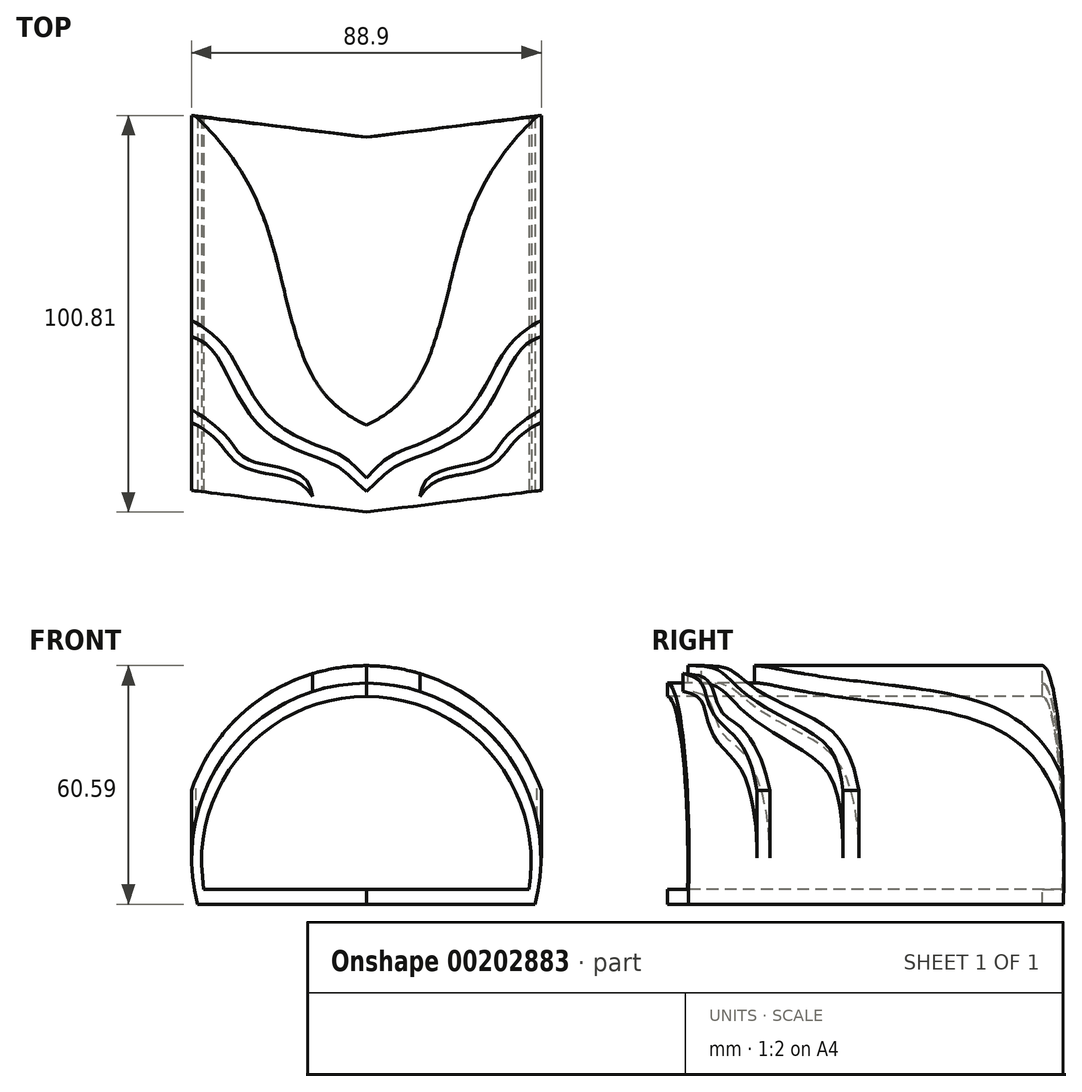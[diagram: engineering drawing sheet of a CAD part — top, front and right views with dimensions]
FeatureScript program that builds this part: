
annotation { "Feature Type Name" : "Feature", "Feature Type Description" : "" }
export const myFeature = defineFeature(function(context is Context, id is Id, definition is map)
    precondition{}
    {
        {
            var Q0;
            Q0=qCreatedBy(makeId("Front.planeOp"),FACE);
            var sketch = newSketch(context, id + "F0", { "sketchPlane" : qUnion([Q0])});
            skLineSegment(sketch, "E0", {"start": v(-42.86, 0) * mm, "end": v(42.86, 0) * mm});
            skArc(sketch, "E1", {"start": v(42.86, 0) * mm, "mid": v(0, 56.22) * mm, "end": v(-42.86, 0) * mm});
            skSolve(sketch);
        }
        {
            var Q0;
            Q0=makeQuery(id+"F0.imprint","IMPRINT",FACE,{"disambiguationData":[TD([[makeQuery(id+"F0.imprint","IMPRINT",EDGE,{"derivedFrom":sQuery(id+"F0.wireOp",EDGE,"E0")}),1.0]])]});
            extrude(context, id + "F1", {"entities" : qUnion([Q0]), "endBound" : BoundingType.SYMMETRIC, "oppositeDirection" : true, "depth" : 101.6 * mm});
        }
        {
            var Q0;
            Q0=qCreatedBy(makeId("Top.planeOp"),FACE);
            cPlane(context, id + "F2", {"entities" : qUnion([Q0]), "cplaneType" : CPlaneType.OFFSET, "offset" : 76.2 * mm, "width" : 152.4 * mm, "height" : 152.4 * mm});
        }
        {
            var Q0;
            Q0=qCreatedBy(id+"F2.planeOp",FACE);
            var sketch = newSketch(context, id + "F3", { "sketchPlane" : qUnion([Q0])});
            skLineSegment(sketch, "E2", {"start": v(-50.8, -44.45) * mm, "end": v(50.8, -44.45) * mm});
            skLineSegment(sketch, "E3", {"start": v(-50.8, -44.45) * mm, "end": v(0, -50.8) * mm});
            skLineSegment(sketch, "E4", {"start": v(0, -50.8) * mm, "end": v(50.8, -44.45) * mm});
            skLineSegment(sketch, "E5", {"start": v(-50.8, 50.8) * mm, "end": v(50.8, 50.8) * mm});
            skLineSegment(sketch, "E6", {"start": v(-50.8, 50.8) * mm, "end": v(0, 44.45) * mm});
            skLineSegment(sketch, "E7", {"start": v(0, 44.45) * mm, "end": v(50.8, 50.8) * mm});
            skLineSegment(sketch, "E8", {"start": v(-50.8, -44.45) * mm, "end": v(-50.8, -60.54) * mm});
            skLineSegment(sketch, "E9", {"start": v(0, -50.8) * mm, "end": v(-68, -50.8) * mm});
            skLineSegment(sketch, "E10", {"start": v(0, -50.8) * mm, "end": v(79.55, -50.8) * mm});
            skLineSegment(sketch, "E11", {"start": v(50.8, -44.45) * mm, "end": v(50.8, -63.1) * mm});
            skSolve(sketch);
        }
        {
            var Q0;
            {var subQ0=sQuery(id+"F3.wireOp",EDGE,"E4");Q0=makeQuery(id+"F3.imprint","IMPRINT",FACE,{"disambiguationData":[TD([[makeQuery(id+"F3.imprint","IMPRINT",EDGE,{"derivedFrom":subQ0}),-1.0]])]});}
            var Q1;
            {var subQ0=sQuery(id+"F3.wireOp",EDGE,"E3");Q1=makeQuery(id+"F3.imprint","IMPRINT",FACE,{"disambiguationData":[TD([[makeQuery(id+"F3.imprint","IMPRINT",EDGE,{"derivedFrom":subQ0}),-1.0]])]});}
            var Q2;
            Q2=makeQuery(id+"F3.imprint","IMPRINT",FACE,{"disambiguationData":[TD([[makeQuery(id+"F3.imprint","IMPRINT",EDGE,{"derivedFrom":sQuery(id+"F3.wireOp",EDGE,"E5")}),-1.0]])]});
            extrude(context, id + "F4", {"entities" : qUnion([Q0, Q1, Q2]), "operationType" : NewBodyOperationType.REMOVE, "endBound" : BoundingType.THROUGH_ALL, "oppositeDirection" : true, "depth" : 25.4 * mm});
        }
        {
            var Q0;
            Q0=qCreatedBy(makeId("Top.planeOp"),FACE);
            cPlane(context, id + "F5", {"entities" : qUnion([Q0]), "cplaneType" : CPlaneType.OFFSET, "offset" : 63.5 * mm, "width" : 152.4 * mm, "height" : 152.4 * mm});
        }
        {
            var Q0;
            Q0=qCreatedBy(makeId("Front.planeOp"),FACE);
            cPlane(context, id + "F6", {"entities" : qUnion([Q0]), "cplaneType" : CPlaneType.OFFSET, "offset" : 63.5 * mm, "width" : 152.4 * mm, "height" : 152.4 * mm});
        }
        {
            var Q0;
            Q0=qCreatedBy(id+"F5.planeOp",FACE);
            var sketch = newSketch(context, id + "F7", { "sketchPlane" : qUnion([Q0])});
            skLineSegment(sketch, "E12", {"start": v(0, 44.45) * mm, "end": v(0, -50.8) * mm, "construction": true});
            skLineSegment(sketch, "E13.bottom", {"start": v(0, -50.8) * mm, "end": v(44.45, -50.8) * mm, "construction": true});
            skLineSegment(sketch, "E13.top", {"start": v(0, 50.8) * mm, "end": v(44.45, 50.8) * mm, "construction": true});
            skLineSegment(sketch, "E13.left", {"start": v(0, -50.8) * mm, "end": v(0, 50.8) * mm, "construction": true});
            skLineSegment(sketch, "E13.right", {"start": v(44.45, -50.8) * mm, "end": v(44.45, 50.8) * mm, "construction": true});
            skFitSpline(sketch, "E14", {"points": [v(0, -28.69) * mm, v(17.05, -8.34) * mm, v(23.1, 14.39) * mm, v(44.45, 50.8) * mm], "startDerivative": vector(102.18, 47.54) * mm, "endDerivative": vector(107.88, 98.84) * mm});
            skLineSegment(sketch, "E15", {"start": v(0, 44.45) * mm, "end": v(43.3, 49.72) * mm, "construction": true});
            skFitSpline(sketch, "E16", {"points": [v(0, -45.55) * mm, v(3.85, -42.07) * mm, v(8.07, -38.77) * mm, v(26.4, -29.6) * mm, v(38.68, -10.17) * mm, v(44.45, -6.14) * mm], "startDerivative": vector(28.52, 26.1) * mm, "endDerivative": vector(36.73, 15.42) * mm});
            skFitSpline(sketch, "E17", {"points": [v(0, -42.07) * mm, v(3.3, -38.77) * mm, v(7.52, -35.83) * mm, v(23.65, -27.59) * mm, v(35.38, -9.62) * mm, v(44.45, -2.1) * mm], "startDerivative": vector(19.75, 23.3) * mm, "endDerivative": vector(48.33, 24.55) * mm});
            skFitSpline(sketch, "E18", {"points": [v(10.43, -20.94) * mm, v(21.08, -12.92) * mm, v(31.17, 3.57) * mm, v(44.45, 12.74) * mm], "startDerivative": vector(37.89, 20.7) * mm, "endDerivative": vector(43.58, 21.64) * mm});
            skFitSpline(sketch, "E19", {"points": [v(13.93, -15.76) * mm, v(19.8, -10.36) * mm, v(27.87, 4.5) * mm, v(44.45, 16.22) * mm], "startDerivative": vector(25.1, 17.01) * mm, "endDerivative": vector(47.74, 24.91) * mm});
            skFitSpline(sketch, "E20", {"points": [v(21.08, 6.33) * mm, v(26.22, 12) * mm, v(28.78, 20.07) * mm, v(36.66, 29.24) * mm, v(44.45, 33.64) * mm], "startDerivative": vector(27.07, 22.58) * mm, "endDerivative": vector(31.22, 14.61) * mm});
            skFitSpline(sketch, "E21", {"points": [v(22.43, 11.8) * mm, v(25.17, 16.63) * mm, v(27.6, 22.21) * mm, v(35.65, 31.39) * mm, v(44.45, 36.2) * mm], "startDerivative": vector(18.51, 3.78) * mm, "endDerivative": vector(31.7, 14.95) * mm});
            skFitSpline(sketch, "E22", {"points": [v(13.66, -46.82) * mm, v(16.5, -43.72) * mm, v(21.78, -41.65) * mm, v(32.07, -38.83) * mm, v(37.76, -32.72) * mm, v(44.45, -27.95) * mm], "startDerivative": vector(18.19, 23.47) * mm, "endDerivative": vector(36.32, 19.04) * mm});
            skFitSpline(sketch, "E23", {"points": [v(13.66, -46.82) * mm, v(14.9, -43) * mm, v(20.92, -39.76) * mm, v(30.81, -37.08) * mm, v(34.72, -32.57) * mm, v(44.45, -24.75) * mm], "startDerivative": vector(6.16, 28.42) * mm, "endDerivative": vector(47.3, 26.68) * mm});
            skLineSegment(sketch, "E24", {"start": v(0, -50.8) * mm, "end": v(0, 44.45) * mm});
            skLineSegment(sketch, "E25", {"start": v(0, 44.45) * mm, "end": v(43.3, 49.72) * mm});
            skLineSegment(sketch, "E26", {"start": v(0, -50.8) * mm, "end": v(44.45, -50.8) * mm});
            skLineSegment(sketch, "E27", {"start": v(44.45, -50.8) * mm, "end": v(44.45, 50.8) * mm});
            skLineSegment(sketch, "E28.MirrorCS", {"start": v(-44.45, -50.8) * mm, "end": v(-44.45, 50.8) * mm});
            skLineSegment(sketch, "E29.MirrorCS", {"start": v(0, -50.8) * mm, "end": v(-44.45, -50.8) * mm});
            skLineSegment(sketch, "E30.MirrorCS", {"start": v(0, 44.45) * mm, "end": v(-43.3, 49.72) * mm});
            skLineSegment(sketch, "E31.MirrorCS", {"start": v(0, 50.8) * mm, "end": v(-44.45, 50.8) * mm, "construction": true});
            skLineSegment(sketch, "E32.MirrorCS", {"start": v(-44.45, -50.8) * mm, "end": v(-44.45, 50.8) * mm, "construction": true});
            skFitSpline(sketch, "E33.MirrorCS", {"points": [v(0, -28.69) * mm, v(-17.05, -8.34) * mm, v(-23.1, 14.39) * mm, v(-44.45, 50.8) * mm], "startDerivative": vector(-102.18, 47.54) * mm, "endDerivative": vector(-107.88, 98.84) * mm});
            skLineSegment(sketch, "E34.MirrorCS", {"start": v(0, -50.8) * mm, "end": v(-44.45, -50.8) * mm, "construction": true});
            skLineSegment(sketch, "E35.MirrorCS", {"start": v(0, 44.45) * mm, "end": v(-43.3, 49.72) * mm, "construction": true});
            skFitSpline(sketch, "E36.MirrorCS", {"points": [v(0, -45.55) * mm, v(-3.85, -42.07) * mm, v(-8.07, -38.77) * mm, v(-26.4, -29.6) * mm, v(-38.68, -10.17) * mm, v(-44.45, -6.14) * mm], "startDerivative": vector(-28.52, 26.1) * mm, "endDerivative": vector(-36.73, 15.42) * mm});
            skFitSpline(sketch, "E37.MirrorCS", {"points": [v(0, -42.07) * mm, v(-3.3, -38.77) * mm, v(-7.52, -35.83) * mm, v(-23.65, -27.59) * mm, v(-35.38, -9.62) * mm, v(-44.45, -2.1) * mm], "startDerivative": vector(-19.75, 23.3) * mm, "endDerivative": vector(-48.33, 24.55) * mm});
            skFitSpline(sketch, "E38.MirrorCS", {"points": [v(-21.08, 6.33) * mm, v(-26.22, 12) * mm, v(-28.78, 20.07) * mm, v(-36.66, 29.24) * mm, v(-44.45, 33.64) * mm], "startDerivative": vector(-27.07, 22.58) * mm, "endDerivative": vector(-31.22, 14.61) * mm});
            skFitSpline(sketch, "E39.MirrorCS", {"points": [v(-22.43, 11.8) * mm, v(-25.17, 16.63) * mm, v(-27.6, 22.21) * mm, v(-35.65, 31.39) * mm, v(-44.45, 36.2) * mm], "startDerivative": vector(-18.51, 3.78) * mm, "endDerivative": vector(-31.7, 14.95) * mm});
            skFitSpline(sketch, "E40.MirrorCS", {"points": [v(-13.66, -46.82) * mm, v(-16.5, -43.72) * mm, v(-21.78, -41.65) * mm, v(-32.07, -38.83) * mm, v(-37.76, -32.72) * mm, v(-44.45, -27.95) * mm], "startDerivative": vector(-18.19, 23.47) * mm, "endDerivative": vector(-36.32, 19.04) * mm});
            skFitSpline(sketch, "E41.MirrorCS", {"points": [v(-13.93, -15.76) * mm, v(-19.8, -10.36) * mm, v(-27.87, 4.5) * mm, v(-44.45, 16.22) * mm], "startDerivative": vector(-25.1, 17.01) * mm, "endDerivative": vector(-47.74, 24.91) * mm});
            skFitSpline(sketch, "E42.MirrorCS", {"points": [v(-13.66, -46.82) * mm, v(-14.9, -43) * mm, v(-20.92, -39.76) * mm, v(-30.81, -37.08) * mm, v(-34.72, -32.57) * mm, v(-44.45, -24.75) * mm], "startDerivative": vector(-6.16, 28.42) * mm, "endDerivative": vector(-47.3, 26.68) * mm});
            skFitSpline(sketch, "E43.MirrorCS", {"points": [v(-10.43, -20.94) * mm, v(-21.08, -12.92) * mm, v(-31.17, 3.57) * mm, v(-44.45, 12.74) * mm], "startDerivative": vector(-37.89, 20.7) * mm, "endDerivative": vector(-43.58, 21.64) * mm});
            skSolve(sketch);
        }
        {
            var Q0;
            {var subQ1=sQuery(id+"F7.wireOp",EDGE,"E14");Q0=makeQuery(id+"F7.imprint","IMPRINT",FACE,{"disambiguationData":[TD([[makeQuery(id+"F7.imprint","IMPRINT",EDGE,{"derivedFrom":subQ1}),1.0]])]});}
            var Q1;
            {var subQ1=sQuery(id+"F7.wireOp",EDGE,"E30.MirrorCS");Q1=makeQuery(id+"F7.imprint","IMPRINT",FACE,{"disambiguationData":[TD([[makeQuery(id+"F7.imprint","IMPRINT",EDGE,{"derivedFrom":subQ1}),1.0]])]});}
            var Q2;
            {var subQ0=sQuery(id+"F7.wireOp",EDGE,"E36.MirrorCS");Q2=makeQuery(id+"F7.imprint","IMPRINT",FACE,{"disambiguationData":[TD([[makeQuery(id+"F7.imprint","IMPRINT",EDGE,{"derivedFrom":subQ0}),-1.0]])]});}
            var Q3;
            {var subQ0=sQuery(id+"F7.wireOp",EDGE,"E40.MirrorCS");Q3=makeQuery(id+"F7.imprint","IMPRINT",FACE,{"disambiguationData":[TD([[makeQuery(id+"F7.imprint","IMPRINT",EDGE,{"derivedFrom":subQ0}),-1.0]])]});}
            var Q4;
            {var subQ0=sQuery(id+"F7.wireOp",EDGE,"E16");Q4=makeQuery(id+"F7.imprint","IMPRINT",FACE,{"disambiguationData":[TD([[makeQuery(id+"F7.imprint","IMPRINT",EDGE,{"derivedFrom":subQ0}),1.0]])]});}
            var Q5;
            {var subQ0=sQuery(id+"F7.wireOp",EDGE,"E22");Q5=makeQuery(id+"F7.imprint","IMPRINT",FACE,{"disambiguationData":[TD([[makeQuery(id+"F7.imprint","IMPRINT",EDGE,{"derivedFrom":subQ0}),1.0]])]});}
            extrude(context, id + "F8", {"entities" : qUnion([Q0, Q1, Q2, Q3, Q4, Q5]), "operationType" : NewBodyOperationType.ADD, "endBound" : BoundingType.UP_TO_NEXT, "oppositeDirection" : true, "depth" : 25.4 * mm});
        }
        {
            var Q0;
            Q0=qCreatedBy(id+"F6.planeOp",FACE);
            var sketch = newSketch(context, id + "F9", { "sketchPlane" : qUnion([Q0])});
            skLineSegment(sketch, "E44", {"start": v(-44.13, -2.54) * mm, "end": v(44.13, -2.54) * mm});
            skArc(sketch, "E45", {"start": v(44.13, -2.54) * mm, "mid": v(0, 60.59) * mm, "end": v(-44.13, -2.54) * mm});
            skLineSegment(sketch, "E46", {"start": v(-42.86, 0) * mm, "end": v(42.86, 0) * mm});
            skArc(sketch, "E47", {"start": v(42.86, 0) * mm, "mid": v(0, 56.22) * mm, "end": v(-42.86, 0) * mm});
            skLineSegment(sketch, "E48.bottom", {"start": v(-54.2, -20.5) * mm, "end": v(50.47, -20.5) * mm});
            skLineSegment(sketch, "E48.top", {"start": v(-54.2, 69.65) * mm, "end": v(50.47, 69.65) * mm});
            skLineSegment(sketch, "E48.left", {"start": v(-54.2, -20.5) * mm, "end": v(-54.2, 69.65) * mm});
            skLineSegment(sketch, "E48.right", {"start": v(50.47, -20.5) * mm, "end": v(50.47, 69.65) * mm});
            skSolve(sketch);
        }
        {
            var Q0;
            Q0=makeQuery(id+"F9.imprint","IMPRINT",FACE,{"disambiguationData":[TD([[makeQuery(id+"F9.imprint","IMPRINT",EDGE,{"derivedFrom":sQuery(id+"F9.wireOp",EDGE,"E44")}),-1.0]])]});
            extrude(context, id + "F10", {"entities" : qUnion([Q0]), "operationType" : NewBodyOperationType.REMOVE, "endBound" : BoundingType.THROUGH_ALL, "oppositeDirection" : true, "depth" : 25.4 * mm});
        }
        {
            var Q0;
            Q0=qCreatedBy(id+"F6.planeOp",FACE);
            var sketch = newSketch(context, id + "F11", { "sketchPlane" : qUnion([Q0])});
            skLineSegment(sketch, "E49", {"start": v(-41.31, 3.81) * mm, "end": v(41.3, 3.81) * mm});
            skArc(sketch, "E50", {"start": v(41.3, 3.81) * mm, "mid": v(0, 52.79) * mm, "end": v(-41.31, 3.81) * mm});
            skLineSegment(sketch, "E51", {"start": v(-42.86, 0) * mm, "end": v(42.86, 0) * mm});
            skArc(sketch, "E52", {"start": v(42.86, 0) * mm, "mid": v(0, 56.22) * mm, "end": v(-42.86, 0) * mm});
            skSolve(sketch);
        }
        {
            var Q0;
            Q0=makeQuery(id+"F11.imprint","IMPRINT",FACE,{"disambiguationData":[TD([[makeQuery(id+"F11.imprint","IMPRINT",EDGE,{"derivedFrom":sQuery(id+"F11.wireOp",EDGE,"E49")}),1.0]])]});
            extrude(context, id + "F12", {"entities" : qUnion([Q0]), "operationType" : NewBodyOperationType.REMOVE, "endBound" : BoundingType.THROUGH_ALL, "oppositeDirection" : true, "depth" : 25.4 * mm});
        }
    });
